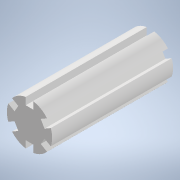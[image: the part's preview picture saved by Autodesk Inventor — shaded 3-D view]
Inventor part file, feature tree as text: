
AUTODESK INVENTOR PART (.ipt)
format: ipt  version: 2021 (Build 250183000, 183)  size: 146,432 bytes
history: native  units: in
note: dims shown in document units (in); Inventor stores cm internally (conversion verified against a paired STEP export)
features: extrude x3, sketch x3
ambient origin geometry x8: Origin, YZ Plane, XZ Plane, XY Plane, X Axis, Y Axis, Z Axis, Center Point
bodies: Solid1 (feature_tree)
feature tree (6):
  extrude  "Extrusion1"  Depth=2.0in TaperAngle=0.0deg
  extrude  "Extrusion2"  Depth=0.5in
  extrude  "Extrusion3"  [1 undecoded]
  sketch  "Sketch1"  dims[d4=2.3622in d6=360.0deg d8=2.0in d9=0.0in]
  sketch  "Sketch2"  dims[d11=2.0in d12=0.0in d13=0.5in]
  sketch  "Sketch3"  dims[d14=2.0in d15=0.0in]
note: 1 required parameter value undecoded (feature->parameter linkage not recoverable at this tier; creation-order binding heuristic only, values carry confidence <= 0.55)
